# Revit family: NLRS_33_GM_FB_TC_STORAX_vloerluik_BV-FL_Thermo_BCB
name_source: partatom
category: Generic Models
revit_build: Autodesk Revit 2014 (Build: 20130308_1515(x64)
units: mm (PartAtom-declared; Revit-internal decimal feet)

## types (7) — shared parameters
Manufacturer = Storax
Model = BV
URL = http://www.storax.nl
belasting = 15 kN
binnenluik = tbv betonvulling
brandwerend 90 min = nee
gasdrukveer = nee
geïsoleerd = ja
materiaal = bcb_staal
productgroep = Vloerluiken
rubberen_afdichting = enkel
scharnierend = nee
sluiting hoek = Yes
vergrendeling = nee
vullen_met_beton = ja
zero-valued in all types: Default Elevation

## per-type parameters (varying)
| type | binnenmaat_breedte | binnenmaat_lengte | gewicht | sluiting | sluiting x-as | sluiting y-as | uitwendige_breedte | uitwendige_lengte |
| maatwerk | 305 mm | 305 mm | 10 | 4 | Yes | Yes | 435 mm | 435 mm |
| BV-FL Thermo 66 | 600 mm | 600 mm | 23 | 4 | Yes | Yes | 730 mm | 730 mm |
| BV-FL Thermo 86 | 600 mm | 800 mm | 29 | 6 | No | Yes | 730 mm | 930 mm |
| BV-FL Thermo 88 | 800 mm | 800 mm | 33 | 8 | Yes | Yes | 930 mm | 930 mm |
| BV-FL Thermo 55 | 500 mm  [stored 1.64042 ft] | 500 mm  [stored 1.64042 ft] | 19 | 8 | No | No | 630 mm  [stored 2.06693 ft] | 630 mm  [stored 2.06693 ft] |
| BV-FL Thermo 106 | 1000 mm  [stored 3.28084 ft] | 600 mm | 33 | 6 | No | Yes | 1130 mm | 730 mm |
| BV-FL Thermo 110 | 1000 mm  [stored 3.28084 ft] | 1000 mm  [stored 3.28084 ft] | 45 | 8 | Yes | Yes | 1130 mm | 1130 mm |

note: [stored X ft] marks values corroborated as IEEE doubles in the binary element streams (Revit-internal decimal feet)

## geometry (parser evidence)
native form markers: Blend x809, Sweep x4
no freeform markers — native parametric forms only
